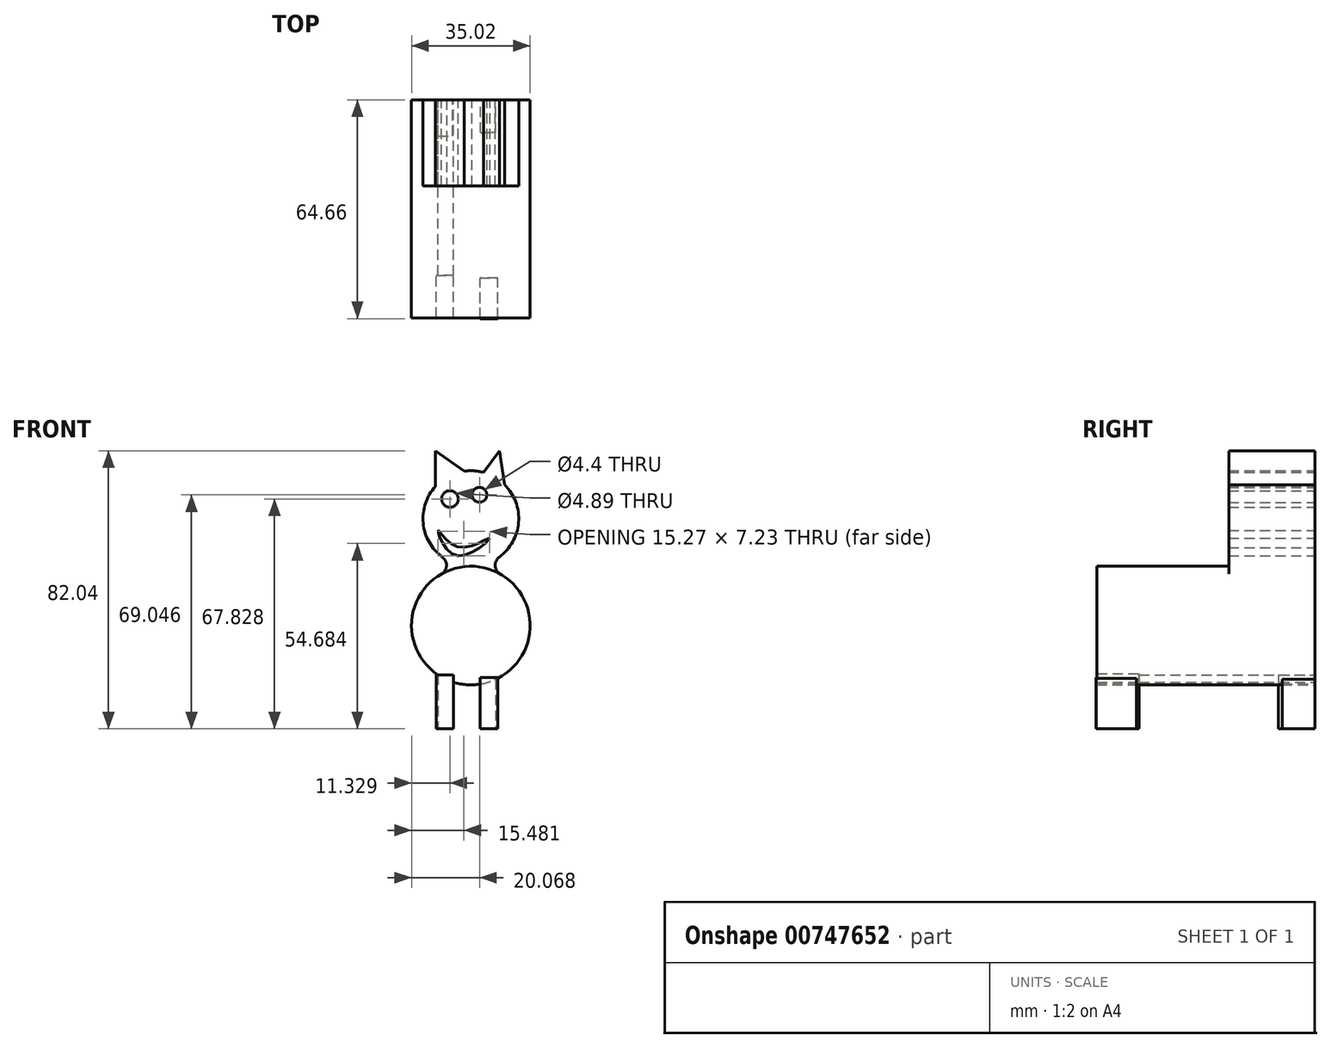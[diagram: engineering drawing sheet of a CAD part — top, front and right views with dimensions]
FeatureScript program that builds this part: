
annotation { "Feature Type Name" : "Feature", "Feature Type Description" : "" }
export const myFeature = defineFeature(function(context is Context, id is Id, definition is map)
    precondition{}
    {
        {
            var Q0;
            Q0=qCreatedBy(makeId("Front.planeOp"),FACE);
            var sketch = newSketch(context, id + "F0", { "sketchPlane" : qUnion([Q0])});
            skCircle(sketch, "E0", {"center": v(0, 0) * mm, "radius": 14.13 * mm});
            skCircle(sketch, "E1", {"center": v(-6.18, 5.79) * mm, "radius": 2.45 * mm});
            skCircle(sketch, "E2", {"center": v(2.56, 7) * mm, "radius": 2.2 * mm});
            skLineSegment(sketch, "E3", {"start": v(-10.47, 9.5) * mm, "end": v(-10.47, 20) * mm});
            skLineSegment(sketch, "E4", {"start": v(-10.47, 20) * mm, "end": v(-1.93, 14) * mm});
            skLineSegment(sketch, "E5", {"start": v(3.72, 13.63) * mm, "end": v(8.45, 20) * mm});
            skLineSegment(sketch, "E6", {"start": v(8.45, 20) * mm, "end": v(10, 9.98) * mm});
            skFitSpline(sketch, "E7", {"points": [v(5.6, -5.79) * mm, v(-3.74, -8.43) * mm, v(-9.64, -3.55) * mm, v(-4.35, -10.86) * mm, v(5.6, -5.79) * mm]});
            skSolve(sketch);
        }
        {
            var Q0;
            Q0=qCreatedBy(makeId("Front.planeOp"),FACE);
            var sketch = newSketch(context, id + "F1", { "sketchPlane" : qUnion([Q0])});
            skCircle(sketch, "E8", {"center": v(0, -31.58) * mm, "radius": 17.51 * mm});
            skLineSegment(sketch, "E9.bottom", {"start": v(-9.74, -46.13) * mm, "end": v(-5.18, -46.13) * mm});
            skLineSegment(sketch, "E9.top", {"start": v(-9.74, -62.85) * mm, "end": v(-5.18, -62.85) * mm});
            skLineSegment(sketch, "E9.left", {"start": v(-9.74, -46.13) * mm, "end": v(-9.74, -62.85) * mm});
            skLineSegment(sketch, "E9.right", {"start": v(-5.18, -46.13) * mm, "end": v(-5.18, -62.85) * mm});
            skLineSegment(sketch, "E10.bottom", {"start": v(6.07, -48) * mm, "end": v(10.05, -48) * mm});
            skLineSegment(sketch, "E10.top", {"start": v(6.07, -62.85) * mm, "end": v(10.05, -62.85) * mm});
            skLineSegment(sketch, "E10.left", {"start": v(6.07, -48) * mm, "end": v(6.07, -62.85) * mm});
            skLineSegment(sketch, "E10.right", {"start": v(10.05, -48) * mm, "end": v(10.05, -62.85) * mm});
            skSolve(sketch);
        }
        {
            var Q0;
            {var subQ0=sQuery(id+"F0.wireOp",EDGE,"E5");Q0=makeQuery(id+"F0.imprint","IMPRINT",FACE,{"disambiguationData":[TD([[makeQuery(id+"F0.imprint","IMPRINT",EDGE,{"derivedFrom":subQ0}),-1.0]])]});}
            var Q1;
            {var subQ0=sQuery(id+"F0.wireOp",EDGE,"E3");Q1=makeQuery(id+"F0.imprint","IMPRINT",FACE,{"disambiguationData":[TD([[makeQuery(id+"F0.imprint","IMPRINT",EDGE,{"derivedFrom":subQ0}),-1.0]])]});}
            var Q2;
            Q2=makeQuery(id+"F0.imprint","IMPRINT",FACE,{"disambiguationData":[TD([[makeQuery(id+"F0.imprint","IMPRINT",EDGE,{"derivedFrom":sQuery(id+"F0.wireOp",EDGE,"E1")}),-1.0]])]});
            extrude(context, id + "F2", {"entities" : qUnion([Q0, Q1, Q2]), "depth" : 25.4 * mm, "offsetDistance" : 25.4 * mm});
        }
        {
            var Q0;
            Q0=qCreatedBy(makeId("Front.planeOp"),FACE);
            var sketch = newSketch(context, id + "F3", { "sketchPlane" : qUnion([Q0])});
            skLineSegment(sketch, "E11.bottom", {"start": v(-9.65, -45.8) * mm, "end": v(-5.38, -45.8) * mm});
            skLineSegment(sketch, "E11.top", {"start": v(-9.65, -62.04) * mm, "end": v(-5.38, -62.04) * mm});
            skLineSegment(sketch, "E11.left", {"start": v(-9.65, -45.8) * mm, "end": v(-9.65, -62.04) * mm});
            skLineSegment(sketch, "E11.right", {"start": v(-5.38, -45.8) * mm, "end": v(-5.38, -62.04) * mm});
            skLineSegment(sketch, "E12.bottom", {"start": v(4.57, -45.8) * mm, "end": v(9.04, -45.8) * mm});
            skLineSegment(sketch, "E12.top", {"start": v(4.57, -62.04) * mm, "end": v(9.04, -62.04) * mm});
            skLineSegment(sketch, "E12.left", {"start": v(4.57, -45.8) * mm, "end": v(4.57, -62.04) * mm});
            skLineSegment(sketch, "E12.right", {"start": v(9.04, -45.8) * mm, "end": v(9.04, -62.04) * mm});
            skSolve(sketch);
        }
        {
            var Q0;
            {var subQ4=sQuery(id+"F1.wireOp",EDGE,"E9.bottom");Q0=makeQuery(id+"F1.imprint","IMPRINT",FACE,{"disambiguationData":[TD([[makeQuery(id+"F1.imprint","IMPRINT",EDGE,{"derivedFrom":subQ4}),1.0]])]});}
            extrude(context, id + "F4", {"entities" : qUnion([Q0]), "operationType" : NewBodyOperationType.ADD, "depth" : 64.4 * mm, "offsetDistance" : 25 * mm});
        }
        {
            var Q0;
            {var subQ0=sQuery(id+"F0.wireOp",EDGE,"E0");Q0=makeQuery(id+"F4.boolean.opBoolean","INTERSECT",EDGE,{"disambiguationData":[OD(0.0)],"derivedFrom":[makeQuery(id+"F2.opExtrude","SWEPT_FACE",FACE,{"disambiguationData":[OSD([subQ0]),TDD([makeQuery(id+"F0.imprint","IMPRINT",EDGE,{"disambiguationData":[TD([[makeQuery(id+"F0.imprint","INTERSECT",VERTEX,{"derivedFrom":[subQ0,sQuery(id+"F0.wireOp",EDGE,"E3")]}),-1.0]])],"derivedFrom":subQ0})])]}),makeQuery(id+"F4.opExtrude","SWEPT_FACE",FACE,{"disambiguationData":[OSD([sQuery(id+"F1.wireOp",EDGE,"E8")])]})]});}
            var Q1;
            {var subQ0=sQuery(id+"F0.wireOp",EDGE,"E0");Q1=makeQuery(id+"F4.boolean.opBoolean","INTERSECT",EDGE,{"disambiguationData":[OD(1.0)],"derivedFrom":[makeQuery(id+"F2.opExtrude","SWEPT_FACE",FACE,{"disambiguationData":[OSD([subQ0]),TDD([makeQuery(id+"F0.imprint","IMPRINT",EDGE,{"disambiguationData":[TD([[makeQuery(id+"F0.imprint","INTERSECT",VERTEX,{"derivedFrom":[subQ0,sQuery(id+"F0.wireOp",EDGE,"E3")]}),-1.0]])],"derivedFrom":subQ0})])]}),makeQuery(id+"F4.opExtrude","SWEPT_FACE",FACE,{"disambiguationData":[OSD([sQuery(id+"F1.wireOp",EDGE,"E8")])]})]});}
            fillet(context, id + "F5", {"entities" : qUnion([Q0, Q1]), "radius" : 3 * mm, "tangentPropagation" : true, "allowEdgeOverflow" : false});
        }
        {
            var Q0;
            Q0=qCreatedBy(makeId("Top.planeOp"),FACE);
            cPlane(context, id + "F6", {"entities" : qUnion([Q0]), "cplaneType" : CPlaneType.OFFSET, "offset" : 62 * mm, "oppositeDirection" : true, "width" : 150 * mm, "height" : 150 * mm});
        }
        {
            var Q0;
            Q0=qCreatedBy(id+"F6.planeOp",FACE);
            var sketch = newSketch(context, id + "F7", { "sketchPlane" : qUnion([Q0])});
            skLineSegment(sketch, "E13.bottom", {"start": v(-17.96, 0) * mm, "end": v(-12.97, 0) * mm});
            skLineSegment(sketch, "E13.top", {"start": v(-17.96, -10.94) * mm, "end": v(-12.97, -10.94) * mm});
            skLineSegment(sketch, "E13.left", {"start": v(-17.96, 0) * mm, "end": v(-17.96, -10.94) * mm});
            skLineSegment(sketch, "E13.right", {"start": v(-12.97, 0) * mm, "end": v(-12.97, -10.94) * mm});
            skSolve(sketch);
        }
        {
            var Q0;
            Q0=makeQuery(id+"F7.imprint","IMPRINT",FACE,{"disambiguationData":[TD([[makeQuery(id+"F7.imprint","IMPRINT",EDGE,{"derivedFrom":sQuery(id+"F7.wireOp",EDGE,"E13.bottom")}),-1.0]])]});
            extrude(context, id + "F8", {"entities" : qUnion([Q0]), "depth" : 16.2 * mm, "offsetDistance" : 25 * mm});
        }
        {
            var Q0;
            Q0=makeQuery(id+"F8.opExtrude","SWEPT_BODY",BODY,{"disambiguationData":[OSD([sQuery(id+"F7.wireOp",EDGE,"E13.bottom"),sQuery(id+"F7.wireOp",EDGE,"E13.top"),sQuery(id+"F7.wireOp",EDGE,"E13.left"),sQuery(id+"F7.wireOp",EDGE,"E13.right")])]});
            deleteBodies(context, id + "F9", {"entities" : qUnion([Q0])});
        }
        {
            var Q0;
            Q0=makeQuery(id+"F3.imprint","IMPRINT",FACE,{"disambiguationData":[TD([[makeQuery(id+"F3.imprint","IMPRINT",EDGE,{"derivedFrom":sQuery(id+"F3.wireOp",EDGE,"E11.bottom")}),-1.0]])]});
            extrude(context, id + "F10", {"entities" : qUnion([Q0]), "operationType" : NewBodyOperationType.ADD, "depth" : 10.7 * mm, "offsetDistance" : 25 * mm});
        }
        {
            var Q0;
            Q0=qCreatedBy(id+"F6.planeOp",FACE);
            var sketch = newSketch(context, id + "F11", { "sketchPlane" : qUnion([Q0])});
            skLineSegment(sketch, "E14.bottom", {"start": v(7.3, 0) * mm, "end": v(2.93, 0) * mm});
            skLineSegment(sketch, "E14.top", {"start": v(7.3, -9.66) * mm, "end": v(2.93, -9.66) * mm});
            skLineSegment(sketch, "E14.left", {"start": v(7.3, 0) * mm, "end": v(7.3, -9.66) * mm});
            skLineSegment(sketch, "E14.right", {"start": v(2.93, 0) * mm, "end": v(2.93, -9.66) * mm});
            skSolve(sketch);
        }
        {
            var Q0;
            Q0 = qSketchRegion(id + "F11", true);
            extrude(context, id + "F12", {"entities" : qUnion([Q0]), "operationType" : NewBodyOperationType.ADD, "depth" : 21.2 * mm, "offsetDistance" : 25 * mm});
        }
        {
            var Q0;
            Q0=qCreatedBy(id+"F6.planeOp",FACE);
            var sketch = newSketch(context, id + "F13", { "sketchPlane" : qUnion([Q0])});
            skLineSegment(sketch, "E15.bottom", {"start": v(-10.18, -64.3) * mm, "end": v(-5.13, -64.3) * mm});
            skLineSegment(sketch, "E15.top", {"start": v(-10.18, -51.86) * mm, "end": v(-5.13, -51.86) * mm});
            skLineSegment(sketch, "E15.left", {"start": v(-10.18, -64.3) * mm, "end": v(-10.18, -51.86) * mm});
            skLineSegment(sketch, "E15.right", {"start": v(-5.13, -64.3) * mm, "end": v(-5.13, -51.86) * mm});
            skSolve(sketch);
        }
        {
            var Q0;
            Q0=makeQuery(id+"F13.imprint","IMPRINT",FACE,{"disambiguationData":[TD([[makeQuery(id+"F13.imprint","IMPRINT",EDGE,{"derivedFrom":sQuery(id+"F13.wireOp",EDGE,"E15.bottom")}),1.0]])]});
            extrude(context, id + "F14", {"entities" : qUnion([Q0]), "operationType" : NewBodyOperationType.ADD, "depth" : 25 * mm, "offsetDistance" : 25 * mm});
        }
        {
            var Q0;
            Q0=qCreatedBy(id+"F6.planeOp",FACE);
            var sketch = newSketch(context, id + "F15", { "sketchPlane" : qUnion([Q0])});
            skLineSegment(sketch, "E16.bottom", {"start": v(2.7, -64.66) * mm, "end": v(7.9, -64.66) * mm});
            skLineSegment(sketch, "E16.top", {"start": v(2.7, -52.67) * mm, "end": v(7.9, -52.67) * mm});
            skLineSegment(sketch, "E16.left", {"start": v(2.7, -64.66) * mm, "end": v(2.7, -52.67) * mm});
            skLineSegment(sketch, "E16.right", {"start": v(7.9, -64.66) * mm, "end": v(7.9, -52.67) * mm});
            skSolve(sketch);
        }
        {
            var Q0;
            Q0=makeQuery(id+"F15.imprint","IMPRINT",FACE,{"disambiguationData":[TD([[makeQuery(id+"F15.imprint","IMPRINT",EDGE,{"derivedFrom":sQuery(id+"F15.wireOp",EDGE,"E16.bottom")}),1.0]])]});
            extrude(context, id + "F16", {"entities" : qUnion([Q0]), "operationType" : NewBodyOperationType.ADD, "depth" : 15.1 * mm, "offsetDistance" : 25 * mm});
        }
    });
